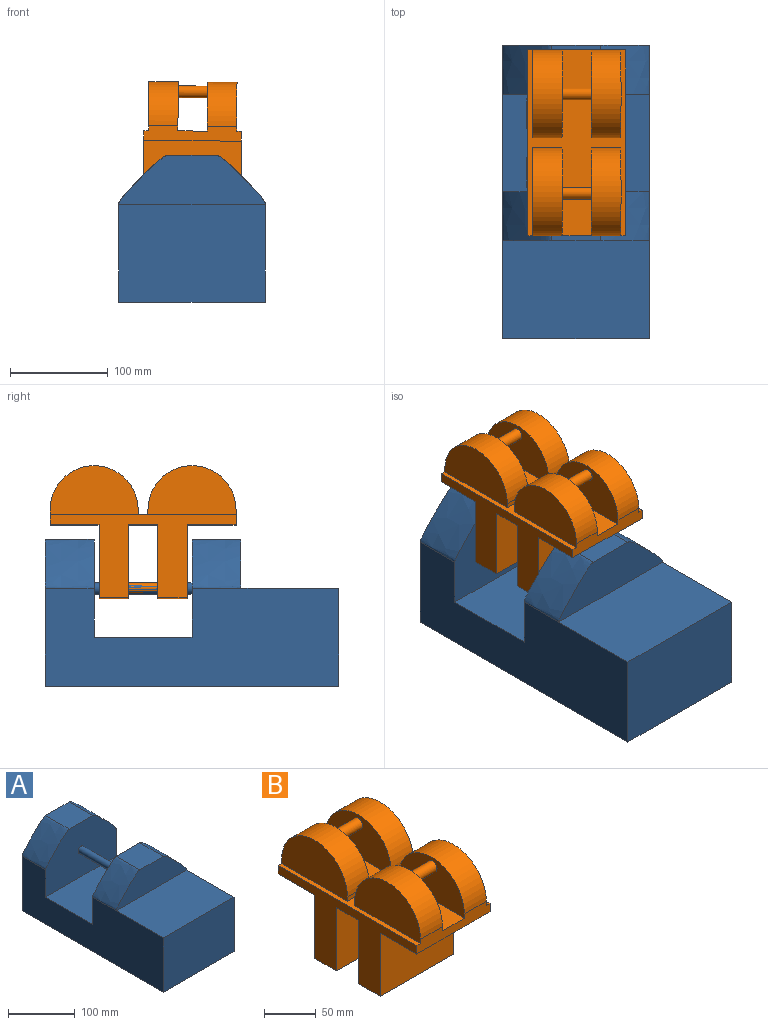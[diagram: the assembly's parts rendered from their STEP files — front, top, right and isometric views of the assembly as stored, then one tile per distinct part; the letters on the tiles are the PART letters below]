
ASSEMBLY  parts=2 mates=1
PART A: 17 faces, bbox 165x317.5x165 mm
  f0: plane 300x100mm, normal (-1,0,0), area 25000mm2, adj f1,f2,f4,f5,f6,f8,f11,f14
  f1: plane 150x100mm, normal (0,0,1), area 15000mm2, adj f0,f2,f3,f9
  f2: plane 150x100mm, normal (0,-1,0), area 15000mm2, adj f0,f1,f3,f5
  f3: plane 300x100mm, normal (1,0,0), area 25000mm2, adj f1,f2,f4,f5,f6,f8,f11,f13
  f4: plane 165.05x165.05mm, normal (0,1,0), area 20383.3mm2, adj f0,f3,f5,f7,f15,f16
  f5: plane 300x150mm, normal (0,0,-1), area 45000mm2, adj f0,f2,f3,f4
  f6: plane 165.05x115.05mm, normal (0,-1,0), area 12809.2mm2, adj f0,f3,f7,f11,f12,f15,f16
  f7: plane 50x50mm, normal (0,0,1), area 2500mm2, adj f4,f6,f15,f16
  f8: plane 165.05x115.05mm, normal (0,1,0), area 12822.4mm2, adj f0,f3,f10,f11,f12,f13,f14
  f9: plane 165.05x65.05mm, normal (0,-1,0), area 5409.4mm2, adj f1,f10,f13,f14
  f10: plane 50x50mm, normal (0,0,1), area 2500mm2, adj f8,f9,f13,f14
  f11: plane 150x100mm, normal (0,0,1), area 15000mm2, adj f0,f3,f6,f8
  f12: cylinder r=6mm len=100mm, axis (0,-1,0), area 3769.9mm2, adj f6,f8
  f13: bspline ~55x50mm, area 3584mm2, adj f3,f8,f9,f10
  f14: bspline ~55x50mm, area 3584mm2, adj f0,f8,f9,f10
  f15: bspline ~55x50mm, area 3584mm2, adj f0,f4,f6,f7
  f16: bspline ~55x50mm, area 3584mm2, adj f3,f4,f6,f7
PART B: 33 faces, bbox 100x190x135 mm
  f0: plane 190x100mm, normal (0,0,1), area 8200mm2, adj f3,f5,f11,f14,f15,f16,f17,f18
  f1: plane 100x75mm, normal (0,1,0), area 7500mm2, adj f3,f5,f6,f13
  f2: plane 100x75mm, normal (0,-1,0), area 7500mm2, adj f3,f5,f8,f12
  f3: plane 190x85mm, normal (-1,0,0), area 6400mm2, adj f0,f1,f2,f4,f6,f7,f8,f10
  f4: plane 100x75mm, normal (0,-1,0), area 7386.9mm2, adj f3,f5,f6,f9,f10
  f5: plane 190x85mm, normal (1,0,0), area 6400mm2, adj f0,f1,f2,f4,f6,f7,f8,f10
  f6: plane 100x30mm, normal (0,0,-1), area 3000mm2, adj f1,f3,f4,f5
  f7: plane 100x75mm, normal (0,1,0), area 7386.9mm2, adj f3,f5,f8,f9,f10
  f8: plane 100x30mm, normal (0,0,-1), area 3000mm2, adj f2,f3,f5,f7
  f9: cylinder r=6mm len=30mm, axis (0,-1,0), area 1131mm2, adj f4,f7
  f10: plane 100x30mm, normal (0,0,-1), area 3000mm2, adj f3,f4,f5,f7
  f11: plane 100x15mm, normal (0,-1,0), area 1300mm2, adj f0,f3,f5,f12,f22,f23,f25,f26
  f12: plane 100x50mm, normal (0,0,-1), area 5000mm2, adj f2,f3,f5,f11
  f13: plane 100x50mm, normal (0,0,-1), area 5000mm2, adj f1,f3,f5,f14
  f14: plane 100x15mm, normal (0,1,0), area 1300mm2, adj f0,f3,f5,f13,f15,f17,f18,f20
  f15: plane 90x50mm, normal (-1,0,0), area 3630.9mm2, adj f0,f14,f16,f32
  f16: plane 30x5mm, normal (0,-1,0), area 150mm2, adj f0,f15,f17,f32
  f17: plane 90x50mm, normal (1,0,0), area 3517.8mm2, adj f0,f14,f16,f27,f32
  f18: plane 90x50mm, normal (-1,0,0), area 3517.8mm2, adj f0,f14,f19,f27,f31
  f19: plane 30x5mm, normal (0,-1,0), area 150mm2, adj f0,f18,f20,f31
  f20: plane 90x50mm, normal (1,0,0), area 3630.9mm2, adj f0,f14,f19,f31
  f21: plane 30x5mm, normal (0,1,0), area 150mm2, adj f0,f22,f23,f30
  f22: plane 90x50mm, normal (-1,0,0), area 3517.8mm2, adj f0,f11,f21,f28,f30
  f23: plane 90x50mm, normal (1,0,0), area 3630.9mm2, adj f0,f11,f21,f30
  f24: plane 30x5mm, normal (0,1,0), area 150mm2, adj f0,f25,f26,f29
  f25: plane 90x50mm, normal (-1,0,0), area 3630.9mm2, adj f0,f11,f24,f29
  f26: plane 90x50mm, normal (1,0,0), area 3517.8mm2, adj f0,f11,f24,f28,f29
  f27: cylinder r=6mm len=30mm, axis (-1,0,0), area 1131mm2, adj f17,f18
  f28: cylinder r=6mm len=30mm, axis (-1,0,0), area 1131mm2, adj f22,f26
  f29: cylinder r=45mm len=90mm, axis (1,0,0), area 4241.2mm2, adj f11,f24,f25,f26
  f30: cylinder r=45mm len=90mm, axis (1,0,0), area 4241.2mm2, adj f11,f21,f22,f23
  f31: cylinder r=45mm len=90mm, axis (1,0,0), area 4241.2mm2, adj f14,f18,f19,f20
  f32: cylinder r=45mm len=90mm, axis (1,0,0), area 4241.2mm2, adj f14,f15,f16,f17
PLACE A at identity fixed
PLACE B rot(axis=(0,1,0),0.5deg) t=(-10.4,0.21,-84.92)mm
MATE revolute A.f12 <-> B.f9  axis (0,-1,0) through (0,51.73,100)mm
